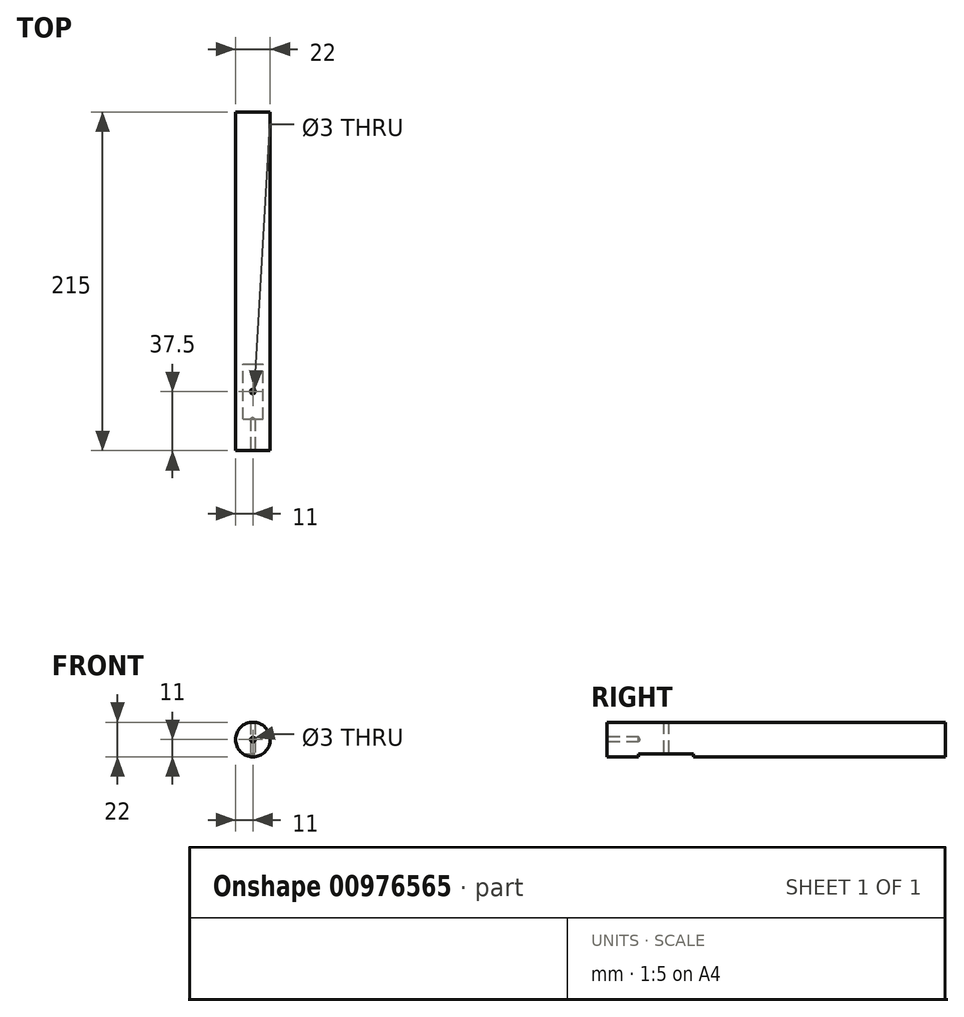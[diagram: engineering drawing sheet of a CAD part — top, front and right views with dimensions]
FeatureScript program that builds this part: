
annotation { "Feature Type Name" : "Feature", "Feature Type Description" : "" }
export const myFeature = defineFeature(function(context is Context, id is Id, definition is map)
    precondition{}
    {
        {
            var Q0;
            Q0=qCreatedBy(makeId("Front.planeOp"),FACE);
            var sketch = newSketch(context, id + "F0", { "sketchPlane" : qUnion([Q0])});
            skCircle(sketch, "E0", {"center": v(0, 11) * mm, "radius": 11 * mm});
            skLineSegment(sketch, "E1", {"start": v(0, 11) * mm, "end": v(0, 0) * mm, "construction": true});
            skLineSegment(sketch, "E2", {"start": v(0, 0) * mm, "end": v(22.65, 0) * mm, "construction": true});
            skSolve(sketch);
        }
        {
            var Q0;
            Q0=makeQuery(id+"F0.imprint","IMPRINT",FACE,{"disambiguationData":[TD([[makeQuery(id+"F0.imprint","IMPRINT",EDGE,{"derivedFrom":sQuery(id+"F0.wireOp",EDGE,"E0")}),1.0]])]});
            extrude(context, id + "F1", {"entities" : qUnion([Q0]), "endBound" : BoundingType.SYMMETRIC, "depth" : 215 * mm, "offsetDistance" : 25 * mm});
        }
        {
            var Q0;
            Q0=makeQuery(id+"F1.opExtrude","CAP_FACE",FACE,{"disambiguationData":[OSD([sQuery(id+"F0.wireOp",EDGE,"E0")])],"isStart":false});
            var sketch = newSketch(context, id + "F2", { "sketchPlane" : qUnion([Q0])});
            skPoint(sketch, "E3", {"position": v(0, 142.1) * mm});
            skPoint(sketch, "E4", {"position": v(0, 11) * mm});
            skSolve(sketch);
        }
        {
            var Q0;
            Q0=sQuery(id+"F2.wireOp",VERTEX,"E4");
            var Q1;
            Q1=makeQuery(id+"F1.opExtrude","SWEPT_BODY",BODY,{"disambiguationData":[OSD([sQuery(id+"F0.wireOp",EDGE,"E0")])]});
            hole(context, id + "F3", {"style" : HoleStyle.SIMPLE, "endStyle" : HoleEndStyle.BLIND, "holeDiameter" : 3 * mm, "majorDiameter" : 5 * mm, "holeDepth" : 20 * mm, "isTappedThrough" : true, "tappedDepth" : 12 * mm, "tapClearance" : 3, "locations" : qUnion([Q0]), "scope" : qUnion([Q1])});
        }
        {
            var Q0;
            Q0=qCreatedBy(makeId("Top.planeOp"),FACE);
            var sketch = newSketch(context, id + "F4", { "sketchPlane" : qUnion([Q0])});
            skPoint(sketch, "E5", {"position": v(0, -70) * mm});
            skSolve(sketch);
        }
        {
            var Q0;
            Q0=sQuery(id+"F4.wireOp",VERTEX,"E5");
            var Q1;
            Q1=makeQuery(id+"F1.opExtrude","SWEPT_BODY",BODY,{"disambiguationData":[OSD([sQuery(id+"F0.wireOp",EDGE,"E0")])]});
            hole(context, id + "F5", {"style" : HoleStyle.SIMPLE, "endStyle" : HoleEndStyle.THROUGH, "oppositeDirection" : true, "holeDiameter" : 3 * mm, "majorDiameter" : 5 * mm, "isTappedThrough" : true, "tappedDepth" : 12 * mm, "tapClearance" : 3, "locations" : qUnion([Q0]), "scope" : qUnion([Q1])});
        }
        {
            var Q0;
            Q0=qCreatedBy(makeId("Right.planeOp"),FACE);
            var sketch = newSketch(context, id + "F6", { "sketchPlane" : qUnion([Q0])});
            skLineSegment(sketch, "E6.bottom", {"start": v(-52.5, 0) * mm, "end": v(-87.5, 0) * mm});
            skLineSegment(sketch, "E6.top", {"start": v(-52.5, 2) * mm, "end": v(-87.5, 2) * mm});
            skLineSegment(sketch, "E6.left", {"start": v(-52.5, 2) * mm, "end": v(-52.5, 0) * mm});
            skLineSegment(sketch, "E6.right", {"start": v(-87.5, 2) * mm, "end": v(-87.5, 0) * mm});
            skLineSegment(sketch, "E7", {"start": v(0, 0) * mm, "end": v(-52.5, 0) * mm, "construction": true});
            skSolve(sketch);
        }
        {
            var Q0;
            Q0 = qSketchRegion(id + "F6", true);
            extrude(context, id + "F7", {"entities" : qUnion([Q0]), "operationType" : NewBodyOperationType.REMOVE, "endBound" : BoundingType.SYMMETRIC, "oppositeDirection" : true, "depth" : 25 * mm, "offsetDistance" : 25 * mm});
        }
    });
